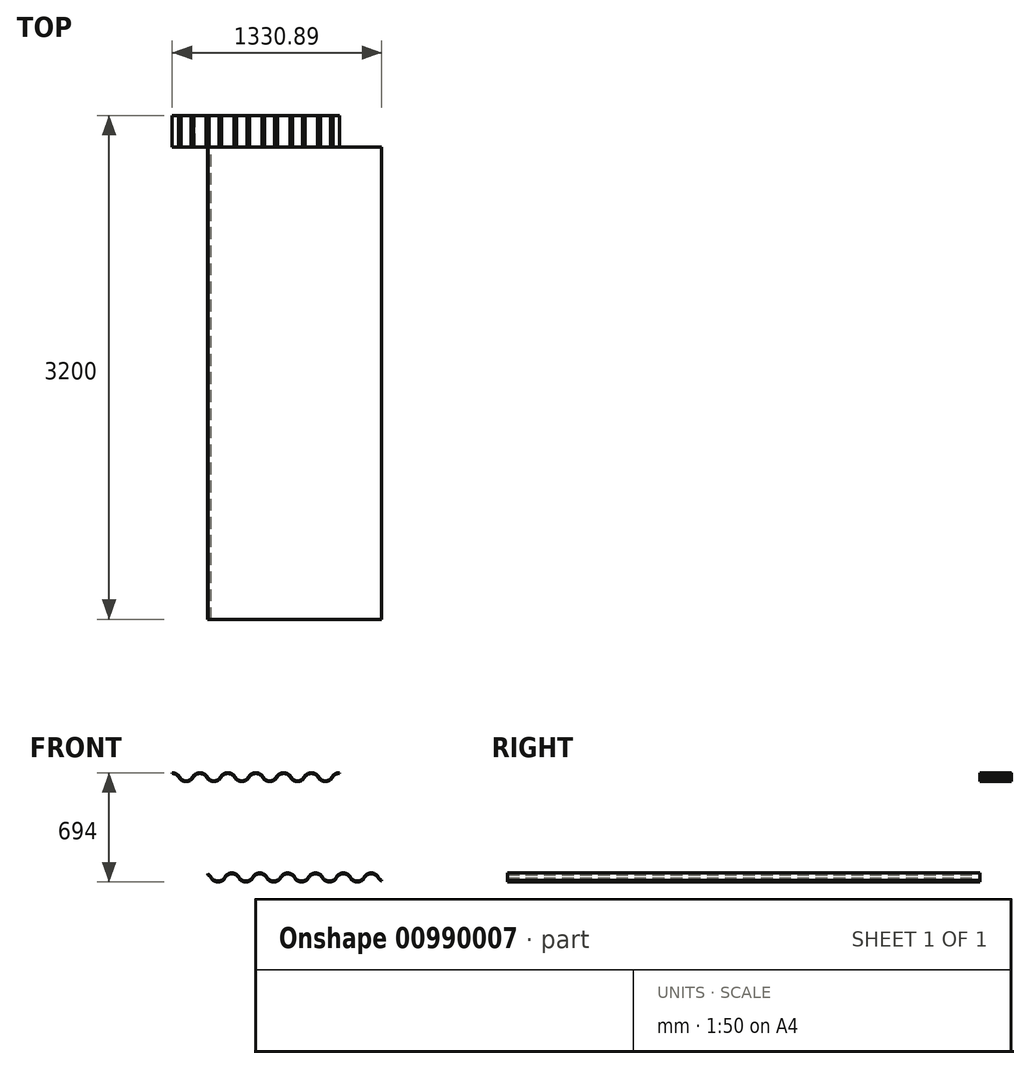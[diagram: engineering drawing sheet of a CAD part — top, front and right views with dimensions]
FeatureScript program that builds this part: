
annotation { "Feature Type Name" : "Feature", "Feature Type Description" : "" }
export const myFeature = defineFeature(function(context is Context, id is Id, definition is map)
    precondition{}
    {
        {
            var Q0;
            Q0=qCreatedBy(makeId("Front.planeOp"),FACE);
            var sketch = newSketch(context, id + "F0", { "sketchPlane" : qUnion([Q0])});
            skArc(sketch, "E0", {"start": v(-30.05, -199.56) * mm, "mid": v(-39.64, -187.35) * mm, "end": v(-52.46, -178.58) * mm});
            skArc(sketch, "E1.MirrorC", {"start": v(58.25, -199.22) * mm, "mid": v(76.93, -180.45) * mm, "end": v(102.5, -173.57) * mm});
            skArc(sketch, "E2.trimOffspring", {"start": v(58.25, -199.22) * mm, "mid": v(14.2, -224.86) * mm, "end": v(-30.05, -199.56) * mm});
            skArc(sketch, "E3", {"start": v(-30.25, -192.93) * mm, "mid": v(-38.77, -181.9) * mm, "end": v(-49.97, -173.57) * mm});
            skArc(sketch, "E4.MirrorC", {"start": v(58.25, -192.93) * mm, "mid": v(76.93, -174.16) * mm, "end": v(102.5, -167.29) * mm});
            skArc(sketch, "E5.trimOffspring", {"start": v(58.25, -192.93) * mm, "mid": v(14, -218.57) * mm, "end": v(-30.25, -192.93) * mm});
            skArc(sketch, "E6.1.0.0", {"start": v(235.25, -192.93) * mm, "mid": v(253.93, -174.16) * mm, "end": v(279.5, -167.29) * mm});
            skArc(sketch, "E6.1.0.1", {"start": v(235.25, -199.22) * mm, "mid": v(253.93, -180.45) * mm, "end": v(279.5, -173.57) * mm});
            skArc(sketch, "E6.1.0.2", {"start": v(235.25, -199.22) * mm, "mid": v(191, -224.86) * mm, "end": v(146.75, -199.22) * mm});
            skArc(sketch, "E6.1.0.3", {"start": v(235.25, -192.93) * mm, "mid": v(191, -218.57) * mm, "end": v(146.75, -192.93) * mm});
            skArc(sketch, "E6.1.0.4", {"start": v(146.75, -199.22) * mm, "mid": v(128.07, -180.45) * mm, "end": v(102.5, -173.57) * mm});
            skArc(sketch, "E6.1.0.5", {"start": v(146.75, -192.93) * mm, "mid": v(128.07, -174.16) * mm, "end": v(102.5, -167.29) * mm});
            skArc(sketch, "E6.2.0.0", {"start": v(412.25, -192.93) * mm, "mid": v(430.93, -174.16) * mm, "end": v(456.5, -167.29) * mm});
            skArc(sketch, "E6.2.0.1", {"start": v(412.25, -199.22) * mm, "mid": v(430.93, -180.45) * mm, "end": v(456.5, -173.57) * mm});
            skArc(sketch, "E6.2.0.2", {"start": v(412.25, -199.22) * mm, "mid": v(368, -224.86) * mm, "end": v(323.75, -199.22) * mm});
            skArc(sketch, "E6.2.0.3", {"start": v(412.25, -192.93) * mm, "mid": v(368, -218.57) * mm, "end": v(323.75, -192.93) * mm});
            skArc(sketch, "E6.2.0.4", {"start": v(323.75, -199.22) * mm, "mid": v(305.07, -180.45) * mm, "end": v(279.5, -173.57) * mm});
            skArc(sketch, "E6.2.0.5", {"start": v(323.75, -192.93) * mm, "mid": v(305.07, -174.16) * mm, "end": v(279.5, -167.29) * mm});
            skArc(sketch, "E6.3.0.0", {"start": v(589.25, -192.93) * mm, "mid": v(607.93, -174.16) * mm, "end": v(633.5, -167.29) * mm});
            skArc(sketch, "E6.3.0.1", {"start": v(589.25, -199.22) * mm, "mid": v(607.93, -180.45) * mm, "end": v(633.5, -173.57) * mm});
            skArc(sketch, "E6.3.0.2", {"start": v(589.25, -199.22) * mm, "mid": v(545, -224.86) * mm, "end": v(500.75, -199.22) * mm});
            skArc(sketch, "E6.3.0.3", {"start": v(589.25, -192.93) * mm, "mid": v(545, -218.57) * mm, "end": v(500.75, -192.93) * mm});
            skArc(sketch, "E6.3.0.4", {"start": v(500.75, -199.22) * mm, "mid": v(482.07, -180.45) * mm, "end": v(456.5, -173.57) * mm});
            skArc(sketch, "E6.3.0.5", {"start": v(500.75, -192.93) * mm, "mid": v(482.07, -174.16) * mm, "end": v(456.5, -167.29) * mm});
            skArc(sketch, "E6.4.0.0", {"start": v(766.25, -192.93) * mm, "mid": v(784.93, -174.16) * mm, "end": v(810.5, -167.29) * mm});
            skArc(sketch, "E6.4.0.1", {"start": v(766.25, -199.22) * mm, "mid": v(784.93, -180.45) * mm, "end": v(810.5, -173.57) * mm});
            skArc(sketch, "E6.4.0.2", {"start": v(766.25, -199.22) * mm, "mid": v(722, -224.86) * mm, "end": v(677.75, -199.22) * mm});
            skArc(sketch, "E6.4.0.3", {"start": v(766.25, -192.93) * mm, "mid": v(722, -218.57) * mm, "end": v(677.75, -192.93) * mm});
            skArc(sketch, "E6.4.0.4", {"start": v(677.75, -199.22) * mm, "mid": v(659.07, -180.45) * mm, "end": v(633.5, -173.57) * mm});
            skArc(sketch, "E6.4.0.5", {"start": v(677.75, -192.93) * mm, "mid": v(659.07, -174.16) * mm, "end": v(633.5, -167.29) * mm});
            skArc(sketch, "E6.5.0.0", {"start": v(943.25, -192.93) * mm, "mid": v(961.93, -174.16) * mm, "end": v(987.5, -167.29) * mm});
            skArc(sketch, "E6.5.0.1", {"start": v(943.25, -199.22) * mm, "mid": v(961.93, -180.45) * mm, "end": v(987.5, -173.57) * mm});
            skArc(sketch, "E6.5.0.2", {"start": v(943.25, -199.22) * mm, "mid": v(899, -224.86) * mm, "end": v(854.75, -199.22) * mm});
            skArc(sketch, "E6.5.0.3", {"start": v(943.25, -192.93) * mm, "mid": v(899, -218.57) * mm, "end": v(854.75, -192.93) * mm});
            skArc(sketch, "E6.5.0.4", {"start": v(854.75, -199.22) * mm, "mid": v(836.07, -180.45) * mm, "end": v(810.5, -173.57) * mm});
            skArc(sketch, "E6.5.0.5", {"start": v(854.75, -192.93) * mm, "mid": v(836.07, -174.16) * mm, "end": v(810.5, -167.29) * mm});
            skArc(sketch, "E6.6.0.2", {"start": v(1051.32, -218.5) * mm, "mid": v(1040.21, -210.2) * mm, "end": v(1031.75, -199.22) * mm});
            skArc(sketch, "E6.6.0.4", {"start": v(1031.75, -199.22) * mm, "mid": v(1013.07, -180.45) * mm, "end": v(987.5, -173.57) * mm});
            skArc(sketch, "E6.6.0.5", {"start": v(1031.75, -192.93) * mm, "mid": v(1013.07, -174.16) * mm, "end": v(987.5, -167.29) * mm});
            skPoint(sketch, "E7.orphan", {"position": v(-74.5, -167.29) * mm});
            skLineSegment(sketch, "E8", {"start": v(1051.32, -218.5) * mm, "end": v(1053.76, -213.47) * mm});
            skArc(sketch, "E9.trimOffspring", {"start": v(1053.76, -213.47) * mm, "mid": v(1041.2, -204.86) * mm, "end": v(1031.75, -192.93) * mm});
            skLineSegment(sketch, "E10", {"start": v(-52.46, -178.58) * mm, "end": v(-49.97, -173.57) * mm});
            skSolve(sketch);
        }
        {
            var Q0;
            Q0 = qSketchRegion(id + "F0", true);
            extrude(context, id + "F1", {"entities" : qUnion([Q0]), "depth" : 25 * mm, "offsetDistance" : 25 * mm});
        }
        {
            var Q0;
            Q0 = qSketchRegion(id + "F0", true);
            extrude(context, id + "F2", {"entities" : qUnion([Q0]), "operationType" : NewBodyOperationType.ADD, "depth" : 3000 * mm, "offsetDistance" : 25 * mm});
        }
        {
            var Q0;
            Q0=qCreatedBy(makeId("Front.planeOp"),FACE);
            var sketch = newSketch(context, id + "F3", { "sketchPlane" : qUnion([Q0])});
            skLineSegment(sketch, "E11.bottom", {"start": v(-277.13, 413.14) * mm, "end": v(-188.63, 413.14) * mm, "construction": true});
            skLineSegment(sketch, "E11.top", {"start": v(-277.13, 464.14) * mm, "end": v(-188.63, 464.14) * mm, "construction": true});
            skLineSegment(sketch, "E11.left", {"start": v(-277.13, 413.14) * mm, "end": v(-277.13, 464.14) * mm, "construction": true});
            skLineSegment(sketch, "E11.right", {"start": v(-188.63, 413.14) * mm, "end": v(-188.63, 464.14) * mm, "construction": true});
            skArc(sketch, "E12", {"start": v(-241.07, 449.2) * mm, "mid": v(-257.61, 460.26) * mm, "end": v(-277.13, 464.14) * mm});
            skArc(sketch, "E13.MirrorC", {"start": v(-136.2, 449.2) * mm, "mid": v(-119.64, 460.26) * mm, "end": v(-100.13, 464.14) * mm});
            skLineSegment(sketch, "E14.MirrorCS", {"start": v(-100.13, 413.14) * mm, "end": v(-188.63, 413.14) * mm, "construction": true});
            skLineSegment(sketch, "E15.MirrorCS", {"start": v(-100.13, 464.14) * mm, "end": v(-188.63, 464.14) * mm, "construction": true});
            skLineSegment(sketch, "E16.MirrorCS", {"start": v(-100.13, 413.14) * mm, "end": v(-100.13, 464.14) * mm, "construction": true});
            skArc(sketch, "E17", {"start": v(-224.83, 427.93) * mm, "mid": v(-188.63, 412.85) * mm, "end": v(-152.42, 427.93) * mm});
            skLineSegment(sketch, "E18", {"start": v(-277.13, 413.14) * mm, "end": v(-241.07, 449.2) * mm});
            skLineSegment(sketch, "E19", {"start": v(-100.13, 413.14) * mm, "end": v(-136.2, 449.2) * mm});
            skLineSegment(sketch, "E20", {"start": v(-241.07, 449.2) * mm, "end": v(-224.83, 427.93) * mm});
            skArc(sketch, "E21.trimOffspring", {"start": v(-152.42, 427.93) * mm, "mid": v(-188.63, 412.85) * mm, "end": v(-224.83, 427.93) * mm});
            skArc(sketch, "E22.trimOffspring", {"start": v(-239.63, 464.14) * mm, "mid": v(-239.63, 464) * mm, "end": v(-239.63, 463.85) * mm});
            skLineSegment(sketch, "E23", {"start": v(-152.42, 427.93) * mm, "end": v(-136.2, 449.2) * mm});
            skArc(sketch, "E24.0", {"start": v(-237.29, 452.5) * mm, "mid": v(-255.54, 464.8) * mm, "end": v(-277.13, 469.14) * mm});
            skArc(sketch, "E24.1", {"start": v(-139.97, 452.5) * mm, "mid": v(-121.72, 464.8) * mm, "end": v(-100.13, 469.14) * mm});
            skLineSegment(sketch, "E24.2", {"start": v(-156.2, 431.23) * mm, "end": v(-139.97, 452.5) * mm});
            skArc(sketch, "E24.3", {"start": v(-156.2, 431.23) * mm, "mid": v(-188.63, 417.85) * mm, "end": v(-221.06, 431.23) * mm});
            skLineSegment(sketch, "E24.4", {"start": v(-237.29, 452.5) * mm, "end": v(-221.06, 431.23) * mm});
            skArc(sketch, "E25.1.0.0", {"start": v(37.03, 452.5) * mm, "mid": v(55.28, 464.8) * mm, "end": v(76.87, 469.14) * mm});
            skArc(sketch, "E25.1.0.1", {"start": v(40.8, 449.2) * mm, "mid": v(57.36, 460.26) * mm, "end": v(76.87, 464.14) * mm});
            skLineSegment(sketch, "E25.1.0.2", {"start": v(20.8, 431.23) * mm, "end": v(37.03, 452.5) * mm});
            skLineSegment(sketch, "E25.1.0.3", {"start": v(24.58, 427.93) * mm, "end": v(40.8, 449.2) * mm});
            skArc(sketch, "E25.1.0.4", {"start": v(24.58, 427.93) * mm, "mid": v(-11.63, 412.85) * mm, "end": v(-47.83, 427.93) * mm});
            skArc(sketch, "E25.1.0.5", {"start": v(20.8, 431.23) * mm, "mid": v(-11.63, 417.85) * mm, "end": v(-44.06, 431.23) * mm});
            skArc(sketch, "E25.1.0.6", {"start": v(-64.07, 449.2) * mm, "mid": v(-80.61, 460.26) * mm, "end": v(-100.13, 464.14) * mm});
            skArc(sketch, "E25.1.0.7", {"start": v(-60.29, 452.5) * mm, "mid": v(-78.54, 464.8) * mm, "end": v(-100.13, 469.14) * mm});
            skLineSegment(sketch, "E25.1.0.8", {"start": v(-64.07, 449.2) * mm, "end": v(-47.83, 427.93) * mm});
            skLineSegment(sketch, "E25.1.0.9", {"start": v(-60.29, 452.5) * mm, "end": v(-44.06, 431.23) * mm});
            skArc(sketch, "E25.2.0.0", {"start": v(214.03, 452.5) * mm, "mid": v(232.28, 464.8) * mm, "end": v(253.87, 469.14) * mm});
            skArc(sketch, "E25.2.0.1", {"start": v(217.8, 449.2) * mm, "mid": v(234.36, 460.26) * mm, "end": v(253.87, 464.14) * mm});
            skLineSegment(sketch, "E25.2.0.2", {"start": v(197.8, 431.23) * mm, "end": v(214.03, 452.5) * mm});
            skLineSegment(sketch, "E25.2.0.3", {"start": v(201.58, 427.93) * mm, "end": v(217.8, 449.2) * mm});
            skArc(sketch, "E25.2.0.4", {"start": v(201.58, 427.93) * mm, "mid": v(165.37, 412.85) * mm, "end": v(129.17, 427.93) * mm});
            skArc(sketch, "E25.2.0.5", {"start": v(197.8, 431.23) * mm, "mid": v(165.37, 417.85) * mm, "end": v(132.94, 431.23) * mm});
            skArc(sketch, "E25.2.0.6", {"start": v(112.93, 449.2) * mm, "mid": v(96.39, 460.26) * mm, "end": v(76.87, 464.14) * mm});
            skArc(sketch, "E25.2.0.7", {"start": v(116.71, 452.5) * mm, "mid": v(98.46, 464.8) * mm, "end": v(76.87, 469.14) * mm});
            skLineSegment(sketch, "E25.2.0.8", {"start": v(112.93, 449.2) * mm, "end": v(129.17, 427.93) * mm});
            skLineSegment(sketch, "E25.2.0.9", {"start": v(116.71, 452.5) * mm, "end": v(132.94, 431.23) * mm});
            skArc(sketch, "E25.3.0.0", {"start": v(391.03, 452.5) * mm, "mid": v(409.28, 464.8) * mm, "end": v(430.87, 469.14) * mm});
            skArc(sketch, "E25.3.0.1", {"start": v(394.8, 449.2) * mm, "mid": v(411.36, 460.26) * mm, "end": v(430.87, 464.14) * mm});
            skLineSegment(sketch, "E25.3.0.2", {"start": v(374.8, 431.23) * mm, "end": v(391.03, 452.5) * mm});
            skLineSegment(sketch, "E25.3.0.3", {"start": v(378.58, 427.93) * mm, "end": v(394.8, 449.2) * mm});
            skArc(sketch, "E25.3.0.4", {"start": v(378.58, 427.93) * mm, "mid": v(342.37, 412.85) * mm, "end": v(306.17, 427.93) * mm});
            skArc(sketch, "E25.3.0.5", {"start": v(374.8, 431.23) * mm, "mid": v(342.37, 417.85) * mm, "end": v(309.94, 431.23) * mm});
            skArc(sketch, "E25.3.0.6", {"start": v(289.93, 449.2) * mm, "mid": v(273.39, 460.26) * mm, "end": v(253.87, 464.14) * mm});
            skArc(sketch, "E25.3.0.7", {"start": v(293.71, 452.5) * mm, "mid": v(275.46, 464.8) * mm, "end": v(253.87, 469.14) * mm});
            skLineSegment(sketch, "E25.3.0.8", {"start": v(289.93, 449.2) * mm, "end": v(306.17, 427.93) * mm});
            skLineSegment(sketch, "E25.3.0.9", {"start": v(293.71, 452.5) * mm, "end": v(309.94, 431.23) * mm});
            skArc(sketch, "E25.4.0.0", {"start": v(568.03, 452.5) * mm, "mid": v(586.28, 464.8) * mm, "end": v(607.87, 469.14) * mm});
            skArc(sketch, "E25.4.0.1", {"start": v(571.8, 449.2) * mm, "mid": v(588.36, 460.26) * mm, "end": v(607.87, 464.14) * mm});
            skLineSegment(sketch, "E25.4.0.2", {"start": v(551.8, 431.23) * mm, "end": v(568.03, 452.5) * mm});
            skLineSegment(sketch, "E25.4.0.3", {"start": v(555.58, 427.93) * mm, "end": v(571.8, 449.2) * mm});
            skArc(sketch, "E25.4.0.4", {"start": v(555.58, 427.93) * mm, "mid": v(519.37, 412.85) * mm, "end": v(483.17, 427.93) * mm});
            skArc(sketch, "E25.4.0.5", {"start": v(551.8, 431.23) * mm, "mid": v(519.37, 417.85) * mm, "end": v(486.94, 431.23) * mm});
            skArc(sketch, "E25.4.0.6", {"start": v(466.93, 449.2) * mm, "mid": v(450.39, 460.26) * mm, "end": v(430.87, 464.14) * mm});
            skArc(sketch, "E25.4.0.7", {"start": v(470.71, 452.5) * mm, "mid": v(452.46, 464.8) * mm, "end": v(430.87, 469.14) * mm});
            skLineSegment(sketch, "E25.4.0.8", {"start": v(466.93, 449.2) * mm, "end": v(483.17, 427.93) * mm});
            skLineSegment(sketch, "E25.4.0.9", {"start": v(470.71, 452.5) * mm, "end": v(486.94, 431.23) * mm});
            skArc(sketch, "E25.5.0.0", {"start": v(745.03, 452.5) * mm, "mid": v(763.28, 464.8) * mm, "end": v(784.87, 469.14) * mm});
            skArc(sketch, "E25.5.0.1", {"start": v(748.8, 449.2) * mm, "mid": v(765.36, 460.26) * mm, "end": v(784.87, 464.14) * mm});
            skLineSegment(sketch, "E25.5.0.2", {"start": v(728.8, 431.23) * mm, "end": v(745.03, 452.5) * mm});
            skLineSegment(sketch, "E25.5.0.3", {"start": v(732.58, 427.93) * mm, "end": v(748.8, 449.2) * mm});
            skArc(sketch, "E25.5.0.4", {"start": v(732.58, 427.93) * mm, "mid": v(696.37, 412.85) * mm, "end": v(660.17, 427.93) * mm});
            skArc(sketch, "E25.5.0.5", {"start": v(728.8, 431.23) * mm, "mid": v(696.37, 417.85) * mm, "end": v(663.94, 431.23) * mm});
            skArc(sketch, "E25.5.0.6", {"start": v(643.93, 449.2) * mm, "mid": v(627.39, 460.26) * mm, "end": v(607.87, 464.14) * mm});
            skArc(sketch, "E25.5.0.7", {"start": v(647.71, 452.5) * mm, "mid": v(629.46, 464.8) * mm, "end": v(607.87, 469.14) * mm});
            skLineSegment(sketch, "E25.5.0.8", {"start": v(643.93, 449.2) * mm, "end": v(660.17, 427.93) * mm});
            skLineSegment(sketch, "E25.5.0.9", {"start": v(647.71, 452.5) * mm, "end": v(663.94, 431.23) * mm});
            skLineSegment(sketch, "E25.direction1", {"start": v(-277.13, 413.14) * mm, "end": v(-100.13, 413.14) * mm, "construction": true});
            skLineSegment(sketch, "E26", {"start": v(-277.13, 464.14) * mm, "end": v(-277.13, 469.14) * mm});
            skLineSegment(sketch, "E27", {"start": v(784.87, 464.14) * mm, "end": v(784.87, 469.14) * mm});
            skSolve(sketch);
        }
        {
            var Q0;
            Q0 = qSketchRegion(id + "F3", true);
            extrude(context, id + "F4", {"entities" : qUnion([Q0]), "oppositeDirection" : true, "depth" : 200 * mm, "offsetDistance" : 25 * mm});
        }
    });
